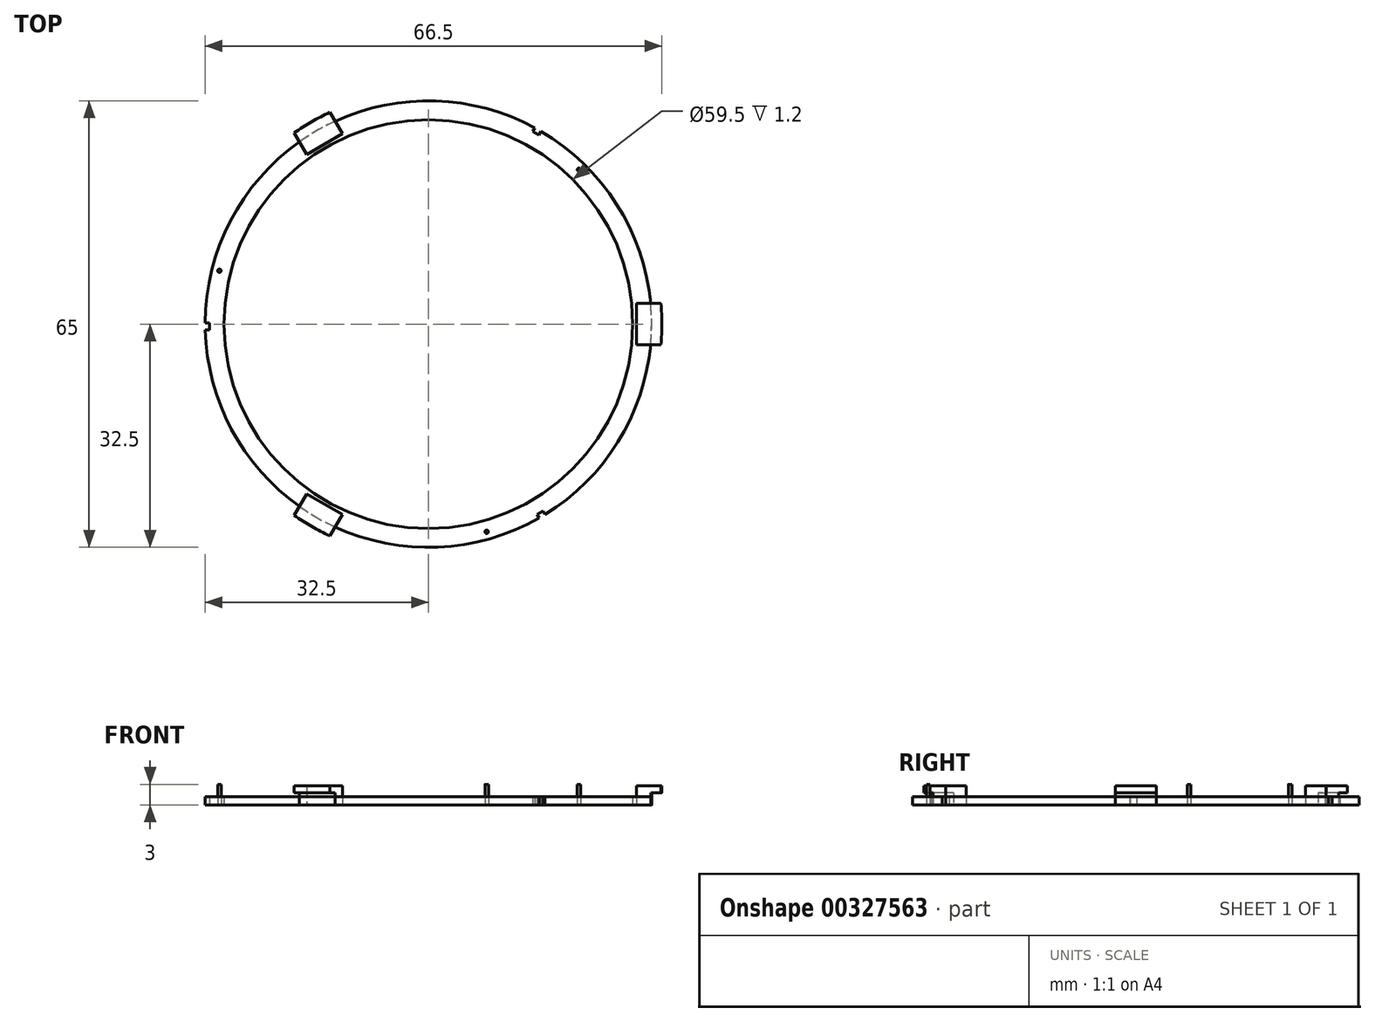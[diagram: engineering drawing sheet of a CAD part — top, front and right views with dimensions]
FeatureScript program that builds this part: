
annotation { "Feature Type Name" : "Feature", "Feature Type Description" : "" }
export const myFeature = defineFeature(function(context is Context, id is Id, definition is map)
    precondition{}
    {
        {
            var Q0;
            Q0=qCreatedBy(makeId("Top.planeOp"),FACE);
            var sketch = newSketch(context, id + "F0", { "sketchPlane" : qUnion([Q0])});
            skCircle(sketch, "E0", {"center": v(0, 0) * mm, "radius": 29.75 * mm});
            skCircle(sketch, "E1", {"center": v(0, 0) * mm, "radius": 32.9 * mm});
            skCircle(sketch, "E2", {"center": v(0, 0) * mm, "radius": 44.5 * mm});
            skLineSegment(sketch, "E3", {"start": v(32.76, 3) * mm, "end": v(30.26, 3) * mm});
            skLineSegment(sketch, "E4", {"start": v(30.26, 3) * mm, "end": v(30.26, -3) * mm});
            skLineSegment(sketch, "E5", {"start": v(30.26, -3) * mm, "end": v(32.76, -3) * mm});
            skLineSegment(sketch, "E6.bottom", {"start": v(30.26, 3) * mm, "end": v(36.26, 3) * mm});
            skLineSegment(sketch, "E6.top", {"start": v(30.26, -3) * mm, "end": v(36.26, -3) * mm});
            skLineSegment(sketch, "E6.right", {"start": v(36.26, 3) * mm, "end": v(36.26, -3) * mm});
            skCircle(sketch, "E7", {"center": v(21.94, 22.47) * mm, "radius": 0.25 * mm});
            skPoint(sketch, "E8", {"position": v(32.9, 0) * mm});
            skLineSegment(sketch, "E9", {"start": v(16.58, 28.41) * mm, "end": v(16.07, 27.54) * mm});
            skLineSegment(sketch, "E10", {"start": v(16.07, 27.54) * mm, "end": v(15.2, 28.04) * mm});
            skLineSegment(sketch, "E11", {"start": v(15.2, 28.04) * mm, "end": v(15.69, 28.92) * mm});
            skCircle(sketch, "E12", {"center": v(0, 0) * mm, "radius": 34 * mm});
            skCircle(sketch, "E13", {"center": v(0, 0) * mm, "radius": 32.5 * mm});
            skSolve(sketch);
        }
        {
            var Q0;
            Q0=makeQuery(id+"F0.imprint","IMPRINT",FACE,{"disambiguationData":[TD([[makeQuery(id+"F0.imprint","IMPRINT",EDGE,{"derivedFrom":sQuery(id+"F0.wireOp",EDGE,"E0")}),-1.0]])]});
            var Q1;
            {var subQ5=sQuery(id+"F0.wireOp",EDGE,"E4");Q1=makeQuery(id+"F0.imprint","IMPRINT",FACE,{"disambiguationData":[TD([[makeQuery(id+"F0.imprint","IMPRINT",EDGE,{"derivedFrom":subQ5}),1.0]])]});}
            var Q2;
            Q2=makeQuery(id+"F0.imprint","IMPRINT",FACE,{"disambiguationData":[TD([[makeQuery(id+"F0.imprint","IMPRINT",EDGE,{"derivedFrom":sQuery(id+"F0.wireOp",EDGE,"E7")}),1.0]])]});
            var Q3;
            {var subQ0=sQuery(id+"F0.wireOp",EDGE,"E9");Q3=makeQuery(id+"F0.imprint","IMPRINT",FACE,{"disambiguationData":[TD([[makeQuery(id+"F0.imprint","IMPRINT",EDGE,{"derivedFrom":subQ0}),-1.0]])]});}
            var Q4;
            {var subQ0=sQuery(id+"F0.wireOp",EDGE,"E11");var subQ1=sQuery(id+"F0.wireOp",EDGE,"E1");var subQ2=makeQuery(id+"F0.imprint","INTERSECT",VERTEX,{"derivedFrom":[subQ1,subQ0]});Q4=makeQuery(id+"F0.imprint","IMPRINT",FACE,{"disambiguationData":[TD([[makeQuery(id+"F0.imprint","IMPRINT",EDGE,{"disambiguationData":[TD([[subQ2,-1.0]])],"derivedFrom":subQ1}),1.0]])]});}
            var Q5;
            {var subQ0=sQuery(id+"F0.wireOp",EDGE,"E9");var subQ1=sQuery(id+"F0.wireOp",EDGE,"E1");var subQ2=makeQuery(id+"F0.imprint","INTERSECT",VERTEX,{"derivedFrom":[subQ1,subQ0]});Q5=makeQuery(id+"F0.imprint","IMPRINT",FACE,{"disambiguationData":[TD([[makeQuery(id+"F0.imprint","IMPRINT",EDGE,{"disambiguationData":[TD([[subQ2,1.0]])],"derivedFrom":subQ1}),1.0]])]});}
            var Q6;
            {var subQ0=sQuery(id+"F0.wireOp",EDGE,"E6.bottom");var subQ1=sQuery(id+"F0.wireOp",EDGE,"E1");var subQ2=makeQuery(id+"F0.imprint","INTERSECT",VERTEX,{"derivedFrom":[subQ1,subQ0]});Q6=makeQuery(id+"F0.imprint","IMPRINT",FACE,{"disambiguationData":[TD([[makeQuery(id+"F0.imprint","IMPRINT",EDGE,{"disambiguationData":[TD([[subQ2,1.0]])],"derivedFrom":subQ1}),1.0]])]});}
            extrude(context, id + "F1", {"entities" : qUnion([Q0, Q1, Q2, Q3, Q4, Q5, Q6]), "depth" : 1.2 * mm});
        }
        {
            var Q0;
            Q0=makeQuery(id+"F0.imprint","IMPRINT",FACE,{"disambiguationData":[TD([[makeQuery(id+"F0.imprint","IMPRINT",EDGE,{"derivedFrom":sQuery(id+"F0.wireOp",EDGE,"E7")}),1.0]])]});
            extrude(context, id + "F2", {"entities" : qUnion([Q0]), "depth" : 3 * mm});
        }
        {
            var Q0;
            {var subQ0=sQuery(id+"F0.wireOp",EDGE,"E6.bottom");var subQ1=sQuery(id+"F0.wireOp",EDGE,"E1");var subQ2=makeQuery(id+"F0.imprint","INTERSECT",VERTEX,{"derivedFrom":[subQ1,subQ0]});Q0=makeQuery(id+"F0.imprint","IMPRINT",FACE,{"disambiguationData":[TD([[makeQuery(id+"F0.imprint","IMPRINT",EDGE,{"disambiguationData":[TD([[subQ2,1.0]])],"derivedFrom":subQ1}),-1.0]])]});}
            var Q1;
            {var subQ5=sQuery(id+"F0.wireOp",EDGE,"E4");Q1=makeQuery(id+"F0.imprint","IMPRINT",FACE,{"disambiguationData":[TD([[makeQuery(id+"F0.imprint","IMPRINT",EDGE,{"derivedFrom":subQ5}),1.0]])]});}
            var Q2;
            {var subQ0=sQuery(id+"F0.wireOp",EDGE,"E6.bottom");var subQ1=sQuery(id+"F0.wireOp",EDGE,"E1");var subQ2=makeQuery(id+"F0.imprint","INTERSECT",VERTEX,{"derivedFrom":[subQ1,subQ0]});Q2=makeQuery(id+"F0.imprint","IMPRINT",FACE,{"disambiguationData":[TD([[makeQuery(id+"F0.imprint","IMPRINT",EDGE,{"disambiguationData":[TD([[subQ2,1.0]])],"derivedFrom":subQ1}),1.0]])]});}
            extrude(context, id + "F3", {"entities" : qUnion([Q0, Q1, Q2]), "depth" : 2.8 * mm});
        }
        {
            var Q0;
            {var subQ0=sQuery(id+"F0.wireOp",EDGE,"E1");var subQ9=makeQuery(id+"F0.imprint","INTERSECT",VERTEX,{"derivedFrom":[subQ0,sQuery(id+"F0.wireOp",EDGE,"E9")]});Q0=makeQuery(id+"F0.imprint","IMPRINT",FACE,{"disambiguationData":[TD([[makeQuery(id+"F0.imprint","IMPRINT",EDGE,{"disambiguationData":[TD([[subQ9,1.0]])],"derivedFrom":subQ0}),-1.0]])]});}
            var Q1;
            {var subQ0=sQuery(id+"F0.wireOp",EDGE,"E6.bottom");var subQ1=sQuery(id+"F0.wireOp",EDGE,"E1");var subQ2=makeQuery(id+"F0.imprint","INTERSECT",VERTEX,{"derivedFrom":[subQ1,subQ0]});Q1=makeQuery(id+"F0.imprint","IMPRINT",FACE,{"disambiguationData":[TD([[makeQuery(id+"F0.imprint","IMPRINT",EDGE,{"disambiguationData":[TD([[subQ2,1.0]])],"derivedFrom":subQ1}),-1.0]])]});}
            var Q2;
            {var subQ0=sQuery(id+"F0.wireOp",EDGE,"E11");var subQ1=sQuery(id+"F0.wireOp",EDGE,"E1");var subQ2=makeQuery(id+"F0.imprint","INTERSECT",VERTEX,{"derivedFrom":[subQ1,subQ0]});Q2=makeQuery(id+"F0.imprint","IMPRINT",FACE,{"disambiguationData":[TD([[makeQuery(id+"F0.imprint","IMPRINT",EDGE,{"disambiguationData":[TD([[subQ2,-1.0]])],"derivedFrom":subQ1}),1.0]])]});}
            var Q3;
            {var subQ0=sQuery(id+"F0.wireOp",EDGE,"E9");var subQ1=sQuery(id+"F0.wireOp",EDGE,"E1");var subQ2=makeQuery(id+"F0.imprint","INTERSECT",VERTEX,{"derivedFrom":[subQ1,subQ0]});Q3=makeQuery(id+"F0.imprint","IMPRINT",FACE,{"disambiguationData":[TD([[makeQuery(id+"F0.imprint","IMPRINT",EDGE,{"disambiguationData":[TD([[subQ2,1.0]])],"derivedFrom":subQ1}),1.0]])]});}
            var Q4;
            {var subQ0=sQuery(id+"F0.wireOp",EDGE,"E6.bottom");var subQ1=sQuery(id+"F0.wireOp",EDGE,"E1");var subQ2=makeQuery(id+"F0.imprint","INTERSECT",VERTEX,{"derivedFrom":[subQ1,subQ0]});Q4=makeQuery(id+"F0.imprint","IMPRINT",FACE,{"disambiguationData":[TD([[makeQuery(id+"F0.imprint","IMPRINT",EDGE,{"disambiguationData":[TD([[subQ2,1.0]])],"derivedFrom":subQ1}),1.0]])]});}
            extrude(context, id + "F4", {"entities" : qUnion([Q0, Q1, Q2, Q3, Q4]), "operationType" : NewBodyOperationType.REMOVE, "depth" : 1.8 * mm});
        }
        {
            var Q0;
            {var subQ0=sQuery(id+"F0.wireOp",EDGE,"E9");Q0=makeQuery(id+"F0.imprint","IMPRINT",FACE,{"disambiguationData":[TD([[makeQuery(id+"F0.imprint","IMPRINT",EDGE,{"derivedFrom":subQ0}),-1.0]])]});}
            extrude(context, id + "F5", {"entities" : qUnion([Q0]), "depth" : 2 * mm});
        }
        {
            var Q0;
            Q0=qCreatedBy(makeId("Front.planeOp"),FACE);
            var sketch = newSketch(context, id + "F6", { "sketchPlane" : qUnion([Q0])});
            skLineSegment(sketch, "E14", {"start": v(0, 57.67) * mm, "end": v(0, -58.24) * mm});
            skSolve(sketch);
        }
        {
            var Q0;
            Q0=makeQuery(id+"F3.opExtrude","SWEPT_BODY",BODY,{"disambiguationData":[OSD([sQuery(id+"F0.wireOp",EDGE,"E6.bottom"),sQuery(id+"F0.wireOp",EDGE,"E6.top"),sQuery(id+"F0.wireOp",EDGE,"E4"),sQuery(id+"F0.wireOp",EDGE,"E12")])]});
            var Q1;
            Q1=makeQuery(id+"F2.opExtrude","SWEPT_BODY",BODY,{"disambiguationData":[OSD([sQuery(id+"F0.wireOp",EDGE,"E7")])]});
            var Q2;
            Q2=makeQuery(id+"F5.opExtrude","SWEPT_BODY",BODY,{"disambiguationData":[OSD([sQuery(id+"F0.wireOp",EDGE,"E1"),sQuery(id+"F0.wireOp",EDGE,"E9"),sQuery(id+"F0.wireOp",EDGE,"E10"),sQuery(id+"F0.wireOp",EDGE,"E11")])]});
            var Q3;
            Q3=sQuery(id+"F6.wireOp",EDGE,"E14");
            circularPattern(context, id + "F7", {"entities" : qUnion([Q0, Q1, Q2]), "axis" : qUnion([Q3]), "angle" : 360 * degree, "instanceCount" : 3, "equalSpace" : true});
        }
        {
            var Q0;
            Q0=makeQuery(id+"F5.opExtrude","SWEPT_BODY",BODY,{"disambiguationData":[OSD([sQuery(id+"F0.wireOp",EDGE,"E1"),sQuery(id+"F0.wireOp",EDGE,"E9"),sQuery(id+"F0.wireOp",EDGE,"E10"),sQuery(id+"F0.wireOp",EDGE,"E11")])]});
            var Q1;
            Q1=makeQuery(id+"F7.opPattern","COPY",BODY,{"derivedFrom":makeQuery(id+"F5.opExtrude","SWEPT_BODY",BODY,{"disambiguationData":[OSD([sQuery(id+"F0.wireOp",EDGE,"E1"),sQuery(id+"F0.wireOp",EDGE,"E9"),sQuery(id+"F0.wireOp",EDGE,"E10"),sQuery(id+"F0.wireOp",EDGE,"E11")])]}),"instanceName":"1"});
            var Q2;
            Q2=makeQuery(id+"F7.opPattern","COPY",BODY,{"derivedFrom":makeQuery(id+"F5.opExtrude","SWEPT_BODY",BODY,{"disambiguationData":[OSD([sQuery(id+"F0.wireOp",EDGE,"E1"),sQuery(id+"F0.wireOp",EDGE,"E9"),sQuery(id+"F0.wireOp",EDGE,"E10"),sQuery(id+"F0.wireOp",EDGE,"E11")])]}),"instanceName":"2"});
            var Q3;
            Q3=makeQuery(id+"F1.opExtrude","SWEPT_BODY",BODY,{"disambiguationData":[OSD([sQuery(id+"F0.wireOp",EDGE,"E0"),sQuery(id+"F0.wireOp",EDGE,"E1")])]});
            booleanBodies(context, id + "F8", {"operationType" : BooleanOperationType.SUBTRACTION, "tools" : qUnion([Q0, Q1, Q2]), "targets" : qUnion([Q3])});
        }
    });
